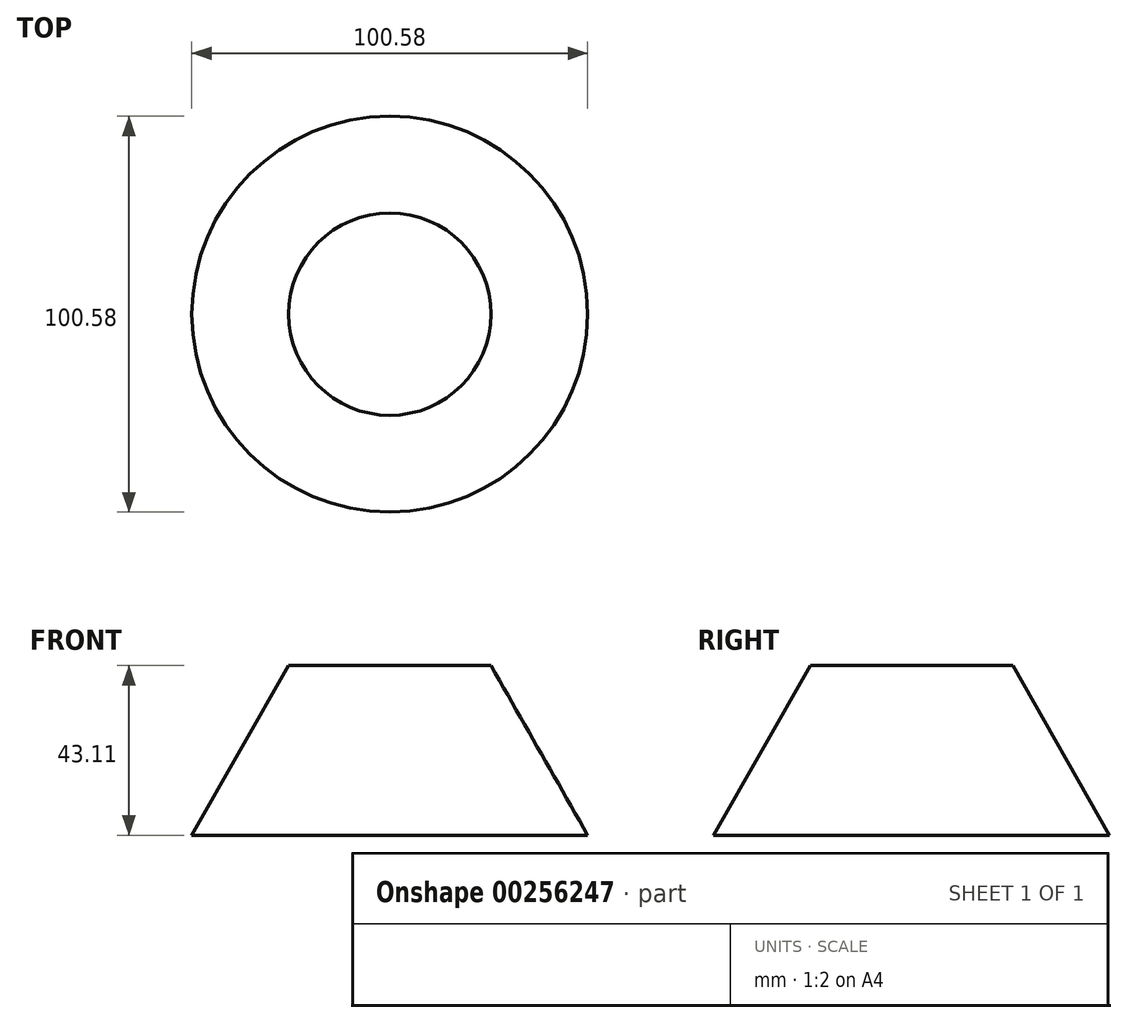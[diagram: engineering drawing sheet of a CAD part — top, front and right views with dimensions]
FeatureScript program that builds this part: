
annotation { "Feature Type Name" : "Feature", "Feature Type Description" : "" }
export const myFeature = defineFeature(function(context is Context, id is Id, definition is map)
    precondition{}
    {
        {
            var Q0;
            Q0=qCreatedBy(makeId("Front.planeOp"),FACE);
            var sketch = newSketch(context, id + "F0", { "sketchPlane" : qUnion([Q0])});
            skLineSegment(sketch, "E0", {"start": v(0, 0) * mm, "end": v(0, 43.1) * mm});
            skLineSegment(sketch, "E1", {"start": v(0, 43.1) * mm, "end": v(25.7, 43.1) * mm});
            skLineSegment(sketch, "E2", {"start": v(25.7, 43.1) * mm, "end": v(50.29, 0) * mm});
            skLineSegment(sketch, "E3", {"start": v(50.29, 0) * mm, "end": v(0, 0) * mm});
            skLineSegment(sketch, "E4", {"start": v(0, 53.33) * mm, "end": v(0, -27.36) * mm, "construction": true});
            skSolve(sketch);
        }
        {
            var Q0;
            Q0=makeQuery(id+"F0.imprint","IMPRINT",FACE,{"disambiguationData":[TD([[makeQuery(id+"F0.imprint","IMPRINT",EDGE,{"derivedFrom":sQuery(id+"F0.wireOp",EDGE,"E0")}),-1.0]])]});
            var Q1;
            Q1=sQuery(id+"F0.wireOp",EDGE,"E4");
            revolve(context, id + "F1", {"entities" : qUnion([Q0]), "axis" : qUnion([Q1]), "revolveType" : RevolveType.FULL});
        }
    });
